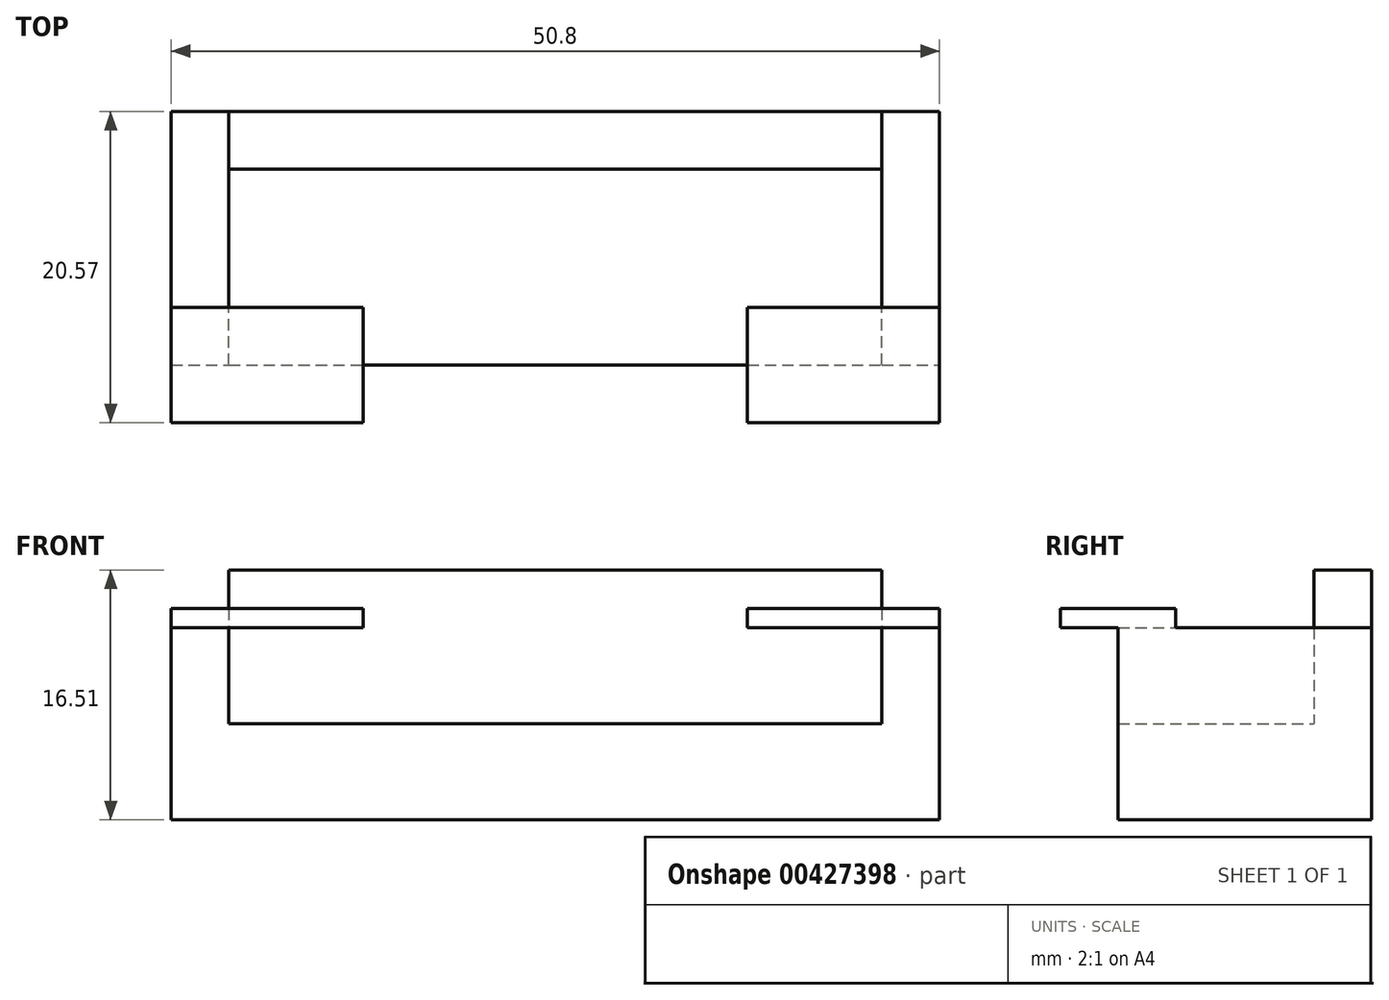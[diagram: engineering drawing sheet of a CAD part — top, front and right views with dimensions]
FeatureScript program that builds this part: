
annotation { "Feature Type Name" : "Feature", "Feature Type Description" : "" }
export const myFeature = defineFeature(function(context is Context, id is Id, definition is map)
    precondition{}
    {
        {
            var Q0;
            Q0=qCreatedBy(makeId("Front.planeOp"),FACE);
            var sketch = newSketch(context, id + "F0", { "sketchPlane" : qUnion([Q0])});
            skLineSegment(sketch, "E0", {"start": v(0, -6.35) * mm, "end": v(-25.4, -6.35) * mm});
            skLineSegment(sketch, "E1", {"start": v(-25.4, -6.35) * mm, "end": v(-25.4, 0) * mm});
            skLineSegment(sketch, "E2.MirrorCS", {"start": v(0, -6.35) * mm, "end": v(25.4, -6.35) * mm});
            skLineSegment(sketch, "E3.MirrorCS", {"start": v(25.4, -6.35) * mm, "end": v(25.4, 0) * mm});
            skLineSegment(sketch, "E4", {"start": v(-25.4, 0) * mm, "end": v(25.4, 0) * mm});
            skSolve(sketch);
        }
        {
            var Q0;
            Q0=qSketchRegion(id+"F0",true);
            extrude(context, id + "F1", {"entities" : qUnion([Q0]), "depth" : 16.76 * mm});
        }
        {
            var Q0;
            Q0=makeQuery(id+"F1.opExtrude","SWEPT_FACE",FACE,{"disambiguationData":[OSD([sQuery(id+"F0.wireOp",EDGE,"E4")])]});
            var sketch = newSketch(context, id + "F2", { "sketchPlane" : qUnion([Q0])});
            skLineSegment(sketch, "E5", {"start": v(-25.4, -16.76) * mm, "end": v(-21.59, -16.76) * mm});
            skLineSegment(sketch, "E6", {"start": v(-21.59, -16.76) * mm, "end": v(-21.59, -3.81) * mm});
            skLineSegment(sketch, "E7", {"start": v(-21.59, -3.81) * mm, "end": v(0, -3.81) * mm});
            skLineSegment(sketch, "E8.MirrorCS", {"start": v(21.59, -3.81) * mm, "end": v(0, -3.81) * mm});
            skLineSegment(sketch, "E9.MirrorCS", {"start": v(21.59, -16.76) * mm, "end": v(21.59, -3.81) * mm});
            skLineSegment(sketch, "E10.MirrorCS", {"start": v(25.4, -16.76) * mm, "end": v(21.59, -16.76) * mm});
            skLineSegment(sketch, "E11", {"start": v(-25.4, -16.76) * mm, "end": v(-25.4, 0) * mm});
            skLineSegment(sketch, "E12", {"start": v(-25.4, 0) * mm, "end": v(25.4, 0) * mm});
            skLineSegment(sketch, "E13", {"start": v(25.4, 0) * mm, "end": v(25.4, -16.76) * mm});
            skSolve(sketch);
        }
        {
            var Q0;
            Q0=qSketchRegion(id+"F2",true);
            extrude(context, id + "F3", {"entities" : qUnion([Q0]), "operationType" : NewBodyOperationType.ADD, "depth" : 6.35 * mm});
        }
        {
            var Q0;
            Q0=makeQuery(id+"F3.opExtrude","CAP_FACE",FACE,{"disambiguationData":[OSD([sQuery(id+"F2.wireOp",EDGE,"E5"),sQuery(id+"F2.wireOp",EDGE,"E6"),sQuery(id+"F2.wireOp",EDGE,"E7"),sQuery(id+"F2.wireOp",EDGE,"E8.MirrorCS"),sQuery(id+"F2.wireOp",EDGE,"E9.MirrorCS"),sQuery(id+"F2.wireOp",EDGE,"E10.MirrorCS"),sQuery(id+"F2.wireOp",EDGE,"E11"),sQuery(id+"F2.wireOp",EDGE,"E12"),sQuery(id+"F2.wireOp",EDGE,"E13")])],"isStart":false});
            var sketch = newSketch(context, id + "F4", { "sketchPlane" : qUnion([Q0])});
            skLineSegment(sketch, "E14", {"start": v(-21.59, -3.81) * mm, "end": v(-21.59, 0) * mm});
            skLineSegment(sketch, "E15", {"start": v(21.59, -3.81) * mm, "end": v(21.59, 0) * mm});
            skLineSegment(sketch, "E16", {"start": v(21.59, 0) * mm, "end": v(-21.59, 0) * mm});
            skLineSegment(sketch, "E17", {"start": v(-21.59, -3.81) * mm, "end": v(21.59, -3.81) * mm});
            skSolve(sketch);
        }
        {
            var Q0;
            Q0=qSketchRegion(id+"F4",true);
            extrude(context, id + "F5", {"entities" : qUnion([Q0]), "operationType" : NewBodyOperationType.ADD, "depth" : 3.8 * mm});
        }
        {
            var Q0;
            {var subQ0=sQuery(id+"F2.wireOp",EDGE,"E12");var subQ1=sQuery(id+"F2.wireOp",EDGE,"E11");var subQ2=sQuery(id+"F2.wireOp",EDGE,"E10.MirrorCS");var subQ3=sQuery(id+"F2.wireOp",EDGE,"E8.MirrorCS");var subQ4=sQuery(id+"F2.wireOp",EDGE,"E7");var subQ5=sQuery(id+"F2.wireOp",EDGE,"E6");var subQ9=sQuery(id+"F0.wireOp",EDGE,"E1");var subQ11=sQuery(id+"F2.wireOp",EDGE,"E5");Q0=makeQuery(id+"F5.boolean.opBoolean","SPLIT",FACE,{"disambiguationData":[TD([makeQuery(id+"F1.opExtrude","SWEPT_FACE",FACE,{"disambiguationData":[OSD([subQ9])]})])],"derivedFrom":makeQuery(id+"F3.opExtrude","CAP_FACE",FACE,{"disambiguationData":[OSD([subQ11,subQ5,subQ4,subQ3,sQuery(id+"F2.wireOp",EDGE,"E9.MirrorCS"),subQ2,subQ1,subQ0,sQuery(id+"F2.wireOp",EDGE,"E13")])],"isStart":false})});}
            var sketch = newSketch(context, id + "F6", { "sketchPlane" : qUnion([Q0])});
            skLineSegment(sketch, "E18", {"start": v(-25.4, -16.76) * mm, "end": v(-25.4, -12.95) * mm});
            skLineSegment(sketch, "E19", {"start": v(-25.4, -16.76) * mm, "end": v(-25.4, -20.57) * mm});
            skLineSegment(sketch, "E20", {"start": v(-25.4, -12.95) * mm, "end": v(-12.7, -12.95) * mm});
            skLineSegment(sketch, "E21", {"start": v(-25.4, -20.57) * mm, "end": v(-12.7, -20.57) * mm});
            skLineSegment(sketch, "E22", {"start": v(-12.7, -20.57) * mm, "end": v(-12.7, -12.95) * mm});
            skSolve(sketch);
        }
        {
            var Q0;
            Q0=qSketchRegion(id+"F6",true);
            extrude(context, id + "F7", {"entities" : qUnion([Q0]), "operationType" : NewBodyOperationType.ADD, "depth" : 1.27 * mm});
        }
        {
            var Q0;
            Q0=makeQuery(id+"F1.opExtrude","SWEPT_BODY",BODY,{"disambiguationData":[OSD([sQuery(id+"F0.wireOp",EDGE,"E0"),sQuery(id+"F0.wireOp",EDGE,"E1"),sQuery(id+"F0.wireOp",EDGE,"E2.MirrorCS"),sQuery(id+"F0.wireOp",EDGE,"E3.MirrorCS"),sQuery(id+"F0.wireOp",EDGE,"E4")])]});
            var Q1;
            Q1=qCreatedBy(makeId("Right.planeOp"),FACE);
            mirror(context, id + "F8", {"operationType" : NewBodyOperationType.ADD, "entities" : qUnion([Q0]), "mirrorPlane" : qUnion([Q1])});
        }
    });
